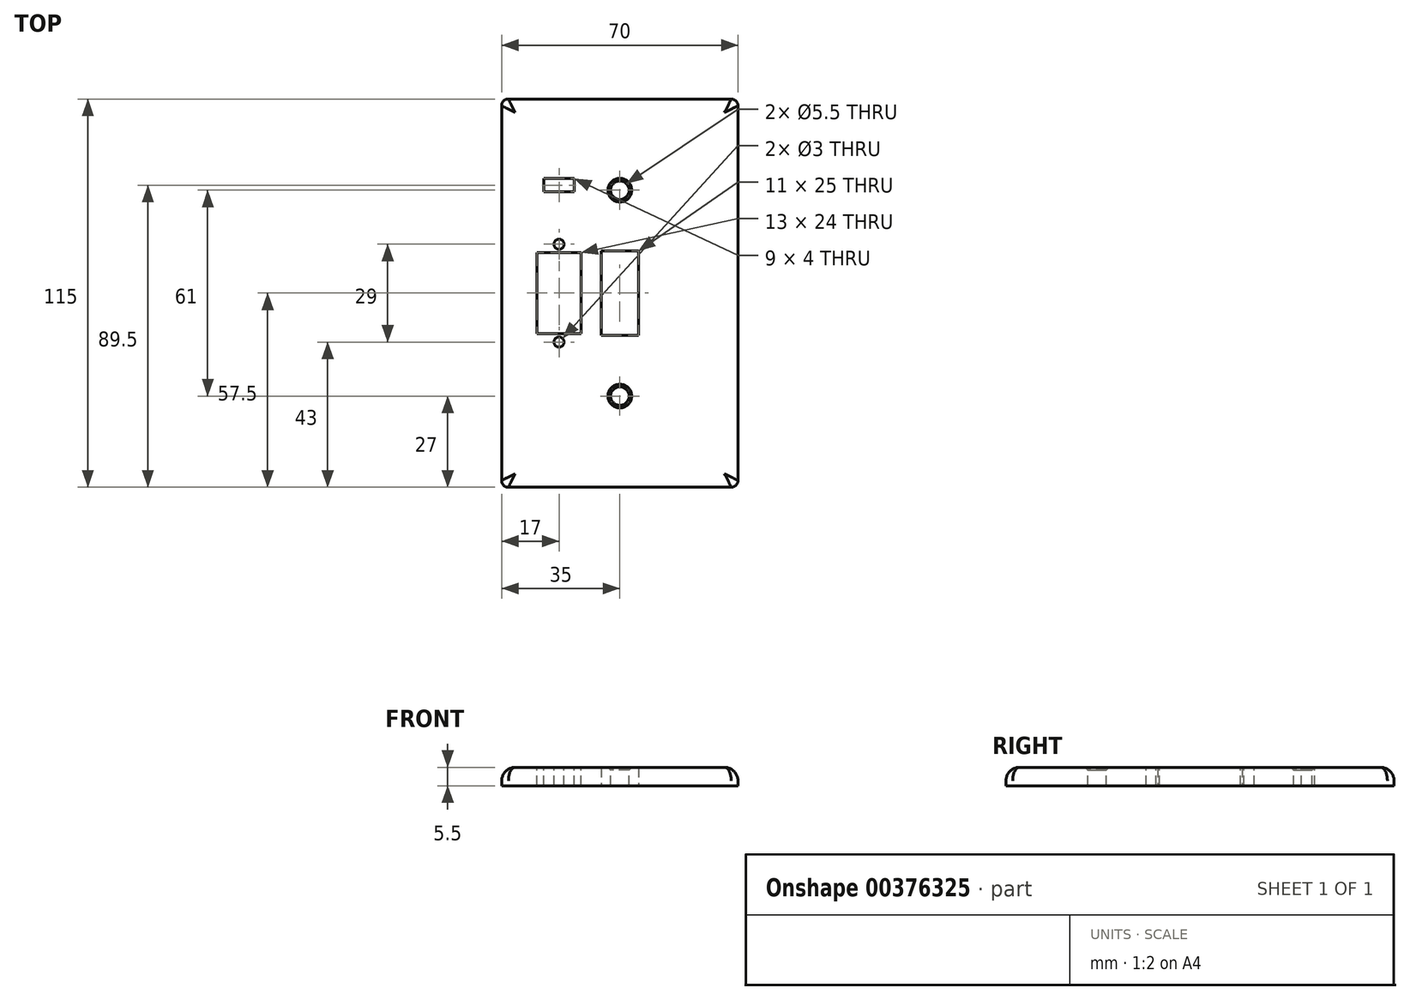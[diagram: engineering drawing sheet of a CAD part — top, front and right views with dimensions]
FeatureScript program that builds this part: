
annotation { "Feature Type Name" : "Feature", "Feature Type Description" : "" }
export const myFeature = defineFeature(function(context is Context, id is Id, definition is map)
    precondition{}
    {
        {
            var Q0;
            Q0=qCreatedBy(makeId("Top.planeOp"),FACE);
            var sketch = newSketch(context, id + "F0", { "sketchPlane" : qUnion([Q0])});
            skLineSegment(sketch, "E0.bottom", {"start": v(35, 57.5) * mm, "end": v(-35, 57.5) * mm});
            skLineSegment(sketch, "E0.top", {"start": v(35, -57.5) * mm, "end": v(-35, -57.5) * mm});
            skLineSegment(sketch, "E0.left", {"start": v(35, 57.5) * mm, "end": v(35, -57.5) * mm});
            skLineSegment(sketch, "E0.right", {"start": v(-35, 57.5) * mm, "end": v(-35, -57.5) * mm});
            skPoint(sketch, "E0.middle", {"position": v(0, 0) * mm});
            skLineSegment(sketch, "E1.bottom", {"start": v(5.5, 12.5) * mm, "end": v(-5.5, 12.5) * mm});
            skLineSegment(sketch, "E1.top", {"start": v(5.5, -12.5) * mm, "end": v(-5.5, -12.5) * mm});
            skLineSegment(sketch, "E1.left", {"start": v(5.5, 12.5) * mm, "end": v(5.5, -12.5) * mm});
            skLineSegment(sketch, "E1.right", {"start": v(-5.5, 12.5) * mm, "end": v(-5.5, -12.5) * mm});
            skSolve(sketch);
        }
        {
            var Q0;
            Q0=makeQuery(id+"F0.imprint","IMPRINT",FACE,{"disambiguationData":[TD([[makeQuery(id+"F0.imprint","IMPRINT",EDGE,{"derivedFrom":sQuery(id+"F0.wireOp",EDGE,"E0.bottom")}),1.0]])]});
            extrude(context, id + "F1", {"entities" : qUnion([Q0]), "depth" : 5.5 * mm});
        }
        {
            var Q0;
            Q0=makeQuery(id+"F1.opExtrude","CAP_FACE",FACE,{"disambiguationData":[OSD([sQuery(id+"F0.wireOp",EDGE,"E0.bottom"),sQuery(id+"F0.wireOp",EDGE,"E0.top"),sQuery(id+"F0.wireOp",EDGE,"E0.left"),sQuery(id+"F0.wireOp",EDGE,"E0.right"),sQuery(id+"F0.wireOp",EDGE,"E1.bottom"),sQuery(id+"F0.wireOp",EDGE,"E1.top"),sQuery(id+"F0.wireOp",EDGE,"E1.left"),sQuery(id+"F0.wireOp",EDGE,"E1.right")])],"isStart":false});
            var sketch = newSketch(context, id + "F2", { "sketchPlane" : qUnion([Q0])});
            skLineSegment(sketch, "E2.bottom", {"start": v(-11.5, 12) * mm, "end": v(-24.5, 12) * mm});
            skLineSegment(sketch, "E2.top", {"start": v(-11.5, -12) * mm, "end": v(-24.5, -12) * mm});
            skLineSegment(sketch, "E2.left", {"start": v(-11.5, 12) * mm, "end": v(-11.5, -12) * mm});
            skLineSegment(sketch, "E2.right", {"start": v(-24.5, 12) * mm, "end": v(-24.5, -12) * mm});
            skPoint(sketch, "E2.middle", {"position": v(-18, 0) * mm});
            skSolve(sketch);
        }
        {
            var Q0;
            Q0=makeQuery(id+"F2.imprint","IMPRINT",FACE,{"disambiguationData":[TD([[makeQuery(id+"F2.imprint","IMPRINT",EDGE,{"derivedFrom":sQuery(id+"F2.wireOp",EDGE,"E2.bottom")}),1.0]])]});
            extrude(context, id + "F3", {"entities" : qUnion([Q0]), "operationType" : NewBodyOperationType.REMOVE, "oppositeDirection" : true, "depth" : 25 * mm});
        }
        {
            var Q0;
            Q0=makeQuery(id+"F1.opExtrude","SWEPT_EDGE",EDGE,{"disambiguationData":[OSD([sQuery(id+"F0.wireOp",EDGE,"E0.top"),sQuery(id+"F0.wireOp",EDGE,"E0.left")])]});
            var Q1;
            Q1=makeQuery(id+"F1.opExtrude","SWEPT_EDGE",EDGE,{"disambiguationData":[OSD([sQuery(id+"F0.wireOp",EDGE,"E0.bottom"),sQuery(id+"F0.wireOp",EDGE,"E0.left")])]});
            var Q2;
            Q2=makeQuery(id+"F1.opExtrude","SWEPT_EDGE",EDGE,{"disambiguationData":[OSD([sQuery(id+"F0.wireOp",EDGE,"E0.top"),sQuery(id+"F0.wireOp",EDGE,"E0.right")])]});
            var Q3;
            Q3=makeQuery(id+"F1.opExtrude","SWEPT_EDGE",EDGE,{"disambiguationData":[OSD([sQuery(id+"F0.wireOp",EDGE,"E0.bottom"),sQuery(id+"F0.wireOp",EDGE,"E0.right")])]});
            fillet(context, id + "F4", {"entities" : qUnion([Q0, Q1, Q2, Q3]), "radius" : 2 * mm, "tangentPropagation" : true, "allowEdgeOverflow" : false});
        }
        {
            var Q0;
            Q0=makeQuery(id+"F1.opExtrude","CAP_EDGE",EDGE,{"disambiguationData":[OSD([sQuery(id+"F0.wireOp",EDGE,"E0.right")])],"isStart":false});
            fillet(context, id + "F5", {"entities" : qUnion([Q0]), "radius" : 4 * mm, "tangentPropagation" : true, "allowEdgeOverflow" : false});
        }
        {
            var Q0;
            Q0=makeQuery(id+"F1.opExtrude","CAP_FACE",FACE,{"disambiguationData":[OSD([sQuery(id+"F0.wireOp",EDGE,"E0.bottom"),sQuery(id+"F0.wireOp",EDGE,"E0.top"),sQuery(id+"F0.wireOp",EDGE,"E0.left"),sQuery(id+"F0.wireOp",EDGE,"E0.right"),sQuery(id+"F0.wireOp",EDGE,"E1.bottom"),sQuery(id+"F0.wireOp",EDGE,"E1.top"),sQuery(id+"F0.wireOp",EDGE,"E1.left"),sQuery(id+"F0.wireOp",EDGE,"E1.right")])],"isStart":false});
            var sketch = newSketch(context, id + "F6", { "sketchPlane" : qUnion([Q0])});
            skPoint(sketch, "E3", {"position": v(0, -30.5) * mm});
            skPoint(sketch, "E4", {"position": v(0, 30.5) * mm});
            skSolve(sketch);
        }
        {
            var Q0;
            Q0=sQuery(id+"F6.wireOp",VERTEX,"E4");
            var Q1;
            Q1=sQuery(id+"F6.wireOp",VERTEX,"E3");
            var Q2;
            Q2=makeQuery(id+"F1.opExtrude","SWEPT_BODY",BODY,{"disambiguationData":[OSD([sQuery(id+"F0.wireOp",EDGE,"E0.bottom"),sQuery(id+"F0.wireOp",EDGE,"E0.top"),sQuery(id+"F0.wireOp",EDGE,"E0.left"),sQuery(id+"F0.wireOp",EDGE,"E0.right"),sQuery(id+"F0.wireOp",EDGE,"E1.bottom"),sQuery(id+"F0.wireOp",EDGE,"E1.top"),sQuery(id+"F0.wireOp",EDGE,"E1.left"),sQuery(id+"F0.wireOp",EDGE,"E1.right")])]});
            hole(context, id + "F7", {"style" : HoleStyle.C_SINK, "endStyle" : HoleEndStyle.THROUGH, "holeDiameter" : 5.5 * mm, "cSinkDiameter" : 7 * mm, "cSinkAngle" : 90 * degree, "isTappedThrough" : true, "tappedDepth" : 12 * mm, "tapClearance" : 3, "locations" : qUnion([Q0, Q1]), "scope" : qUnion([Q2])});
        }
        {
            var Q0;
            Q0=makeQuery(id+"F1.opExtrude","CAP_FACE",FACE,{"disambiguationData":[OSD([sQuery(id+"F0.wireOp",EDGE,"E0.bottom"),sQuery(id+"F0.wireOp",EDGE,"E0.top"),sQuery(id+"F0.wireOp",EDGE,"E0.left"),sQuery(id+"F0.wireOp",EDGE,"E0.right"),sQuery(id+"F0.wireOp",EDGE,"E1.bottom"),sQuery(id+"F0.wireOp",EDGE,"E1.top"),sQuery(id+"F0.wireOp",EDGE,"E1.left"),sQuery(id+"F0.wireOp",EDGE,"E1.right")])],"isStart":false});
            var sketch = newSketch(context, id + "F8", { "sketchPlane" : qUnion([Q0])});
            skPoint(sketch, "E5", {"position": v(-18, 14.5) * mm});
            skPoint(sketch, "E5.positionSnap0", {"position": v(-18, 12) * mm});
            skPoint(sketch, "E6", {"position": v(-18, -14.5) * mm});
            skPoint(sketch, "E6.positionSnap0", {"position": v(-18, -12) * mm});
            skSolve(sketch);
        }
        {
            var Q0;
            Q0=sQuery(id+"F8.wireOp",VERTEX,"E5");
            var Q1;
            Q1=sQuery(id+"F8.wireOp",VERTEX,"E6");
            var Q2;
            Q2=makeQuery(id+"F1.opExtrude","SWEPT_BODY",BODY,{"disambiguationData":[OSD([sQuery(id+"F0.wireOp",EDGE,"E0.bottom"),sQuery(id+"F0.wireOp",EDGE,"E0.top"),sQuery(id+"F0.wireOp",EDGE,"E0.left"),sQuery(id+"F0.wireOp",EDGE,"E0.right"),sQuery(id+"F0.wireOp",EDGE,"E1.bottom"),sQuery(id+"F0.wireOp",EDGE,"E1.top"),sQuery(id+"F0.wireOp",EDGE,"E1.left"),sQuery(id+"F0.wireOp",EDGE,"E1.right")])]});
            hole(context, id + "F9", {"style" : HoleStyle.SIMPLE, "endStyle" : HoleEndStyle.THROUGH, "holeDiameter" : 3 * mm, "isTappedThrough" : true, "tappedDepth" : 12 * mm, "tapClearance" : 3, "locations" : qUnion([Q0, Q1]), "scope" : qUnion([Q2])});
        }
        {
            var Q0;
            Q0=makeQuery(id+"F1.opExtrude","CAP_FACE",FACE,{"disambiguationData":[OSD([sQuery(id+"F0.wireOp",EDGE,"E0.bottom"),sQuery(id+"F0.wireOp",EDGE,"E0.top"),sQuery(id+"F0.wireOp",EDGE,"E0.left"),sQuery(id+"F0.wireOp",EDGE,"E0.right"),sQuery(id+"F0.wireOp",EDGE,"E1.bottom"),sQuery(id+"F0.wireOp",EDGE,"E1.top"),sQuery(id+"F0.wireOp",EDGE,"E1.left"),sQuery(id+"F0.wireOp",EDGE,"E1.right")])],"isStart":false});
            var sketch = newSketch(context, id + "F10", { "sketchPlane" : qUnion([Q0])});
            skLineSegment(sketch, "E7.bottom", {"start": v(-13.5, 34) * mm, "end": v(-22.5, 34) * mm});
            skLineSegment(sketch, "E7.top", {"start": v(-13.5, 30) * mm, "end": v(-22.5, 30) * mm});
            skLineSegment(sketch, "E7.left", {"start": v(-13.5, 34) * mm, "end": v(-13.5, 30) * mm});
            skLineSegment(sketch, "E7.right", {"start": v(-22.5, 34) * mm, "end": v(-22.5, 30) * mm});
            skPoint(sketch, "E7.middle", {"position": v(-18, 32) * mm});
            skPoint(sketch, "E7.middle.positionSnap0", {"position": v(-18, 12) * mm});
            skPoint(sketch, "E7.centerSnap0", {"position": v(-18, 12) * mm});
            skSolve(sketch);
        }
        {
            var Q0;
            Q0=makeQuery(id+"F10.imprint","IMPRINT",FACE,{"disambiguationData":[TD([[makeQuery(id+"F10.imprint","IMPRINT",EDGE,{"derivedFrom":sQuery(id+"F10.wireOp",EDGE,"E7.bottom")}),1.0]])]});
            extrude(context, id + "F11", {"entities" : qUnion([Q0]), "operationType" : NewBodyOperationType.REMOVE, "oppositeDirection" : true, "depth" : 25 * mm});
        }
    });
